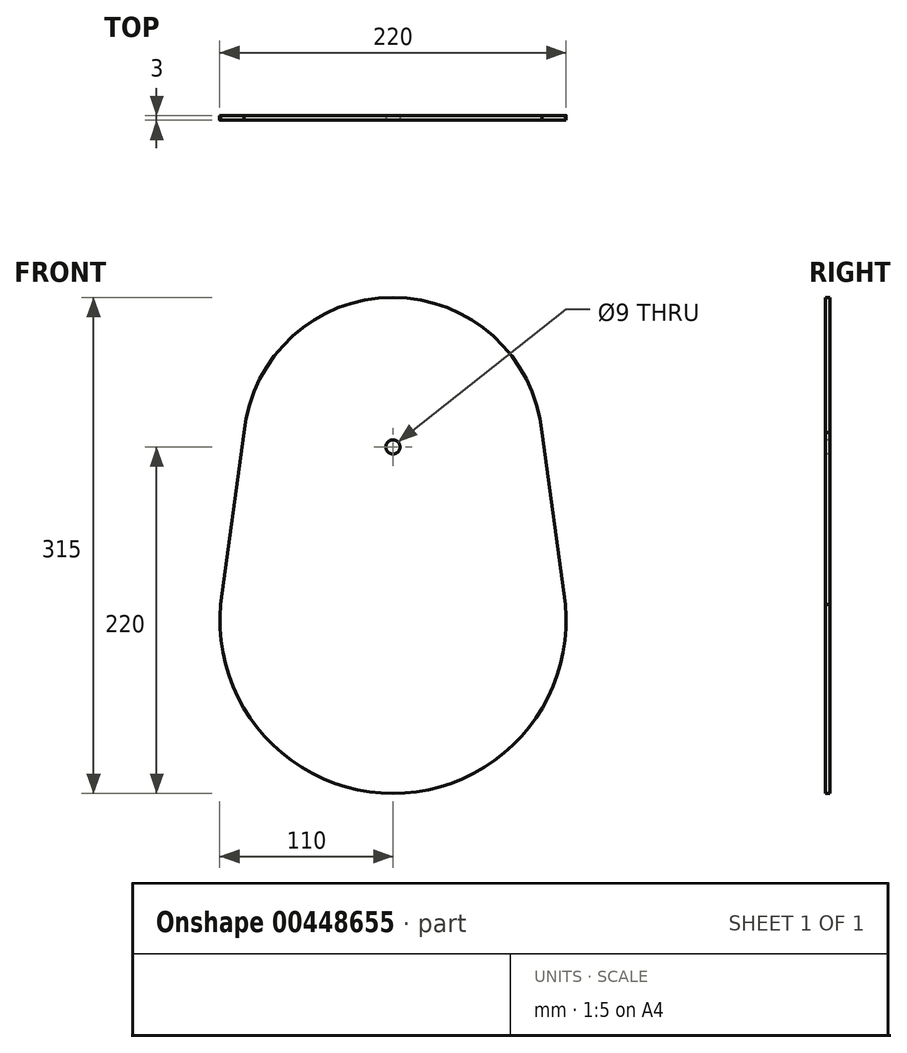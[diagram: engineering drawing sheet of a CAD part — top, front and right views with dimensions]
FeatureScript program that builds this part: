
annotation { "Feature Type Name" : "Feature", "Feature Type Description" : "" }
export const myFeature = defineFeature(function(context is Context, id is Id, definition is map)
    precondition{}
    {
        {
            var Q0;
            Q0=qCreatedBy(makeId("Front.planeOp"),FACE);
            var sketch = newSketch(context, id + "F0", { "sketchPlane" : qUnion([Q0])});
            skArc(sketch, "E0", {"start": v(94.56, 9.1) * mm, "mid": v(0, 95) * mm, "end": v(-94.56, 9.1) * mm});
            skArc(sketch, "E1", {"start": v(-108.2, -90.2) * mm, "mid": v(0, -220) * mm, "end": v(108.2, -90.2) * mm});
            skLineSegment(sketch, "E2", {"start": v(-94.56, 9.1) * mm, "end": v(-109.53, -99.88) * mm});
            skLineSegment(sketch, "E3.MirrorCS", {"start": v(94.56, 9.1) * mm, "end": v(109.53, -99.88) * mm});
            skLineSegment(sketch, "E4", {"start": v(-95, -165.45) * mm, "end": v(95, -165.45) * mm, "construction": true});
            skLineSegment(sketch, "E5", {"start": v(0, -165.45) * mm, "end": v(0, -220) * mm, "construction": true});
            skLineSegment(sketch, "E6", {"start": v(0, -110) * mm, "end": v(0, -165.45) * mm, "construction": true});
            skSolve(sketch);
        }
        {
            var Q0;
            {var subQ1=sQuery(id+"F0.wireOp",EDGE,"E0");Q0=makeQuery(id+"F0.imprint","IMPRINT",FACE,{"disambiguationData":[TD([[makeQuery(id+"F0.imprint","IMPRINT",EDGE,{"derivedFrom":subQ1}),1.0]])]});}
            extrude(context, id + "F1", {"entities" : qUnion([Q0]), "depth" : 3 * mm});
        }
        {
            var Q0;
            Q0=makeQuery(id+"F1.opExtrude","CAP_FACE",FACE,{"disambiguationData":[OSD([sQuery(id+"F0.wireOp",EDGE,"E0"),sQuery(id+"F0.wireOp",EDGE,"E1"),sQuery(id+"F0.wireOp",EDGE,"E2"),sQuery(id+"F0.wireOp",EDGE,"E3.MirrorCS")])],"isStart":false});
            var sketch = newSketch(context, id + "F2", { "sketchPlane" : qUnion([Q0])});
            skCircle(sketch, "E7", {"center": v(0, 0) * mm, "radius": 4.5 * mm});
            skSolve(sketch);
        }
        {
            var Q0;
            Q0=makeQuery(id+"F2.imprint","IMPRINT",FACE,{"disambiguationData":[TD([[makeQuery(id+"F2.imprint","IMPRINT",EDGE,{"derivedFrom":sQuery(id+"F2.wireOp",EDGE,"E7")}),1.0]])]});
            extrude(context, id + "F3", {"entities" : qUnion([Q0]), "operationType" : NewBodyOperationType.REMOVE, "endBound" : BoundingType.THROUGH_ALL, "oppositeDirection" : true, "depth" : 25 * mm});
        }
    });
